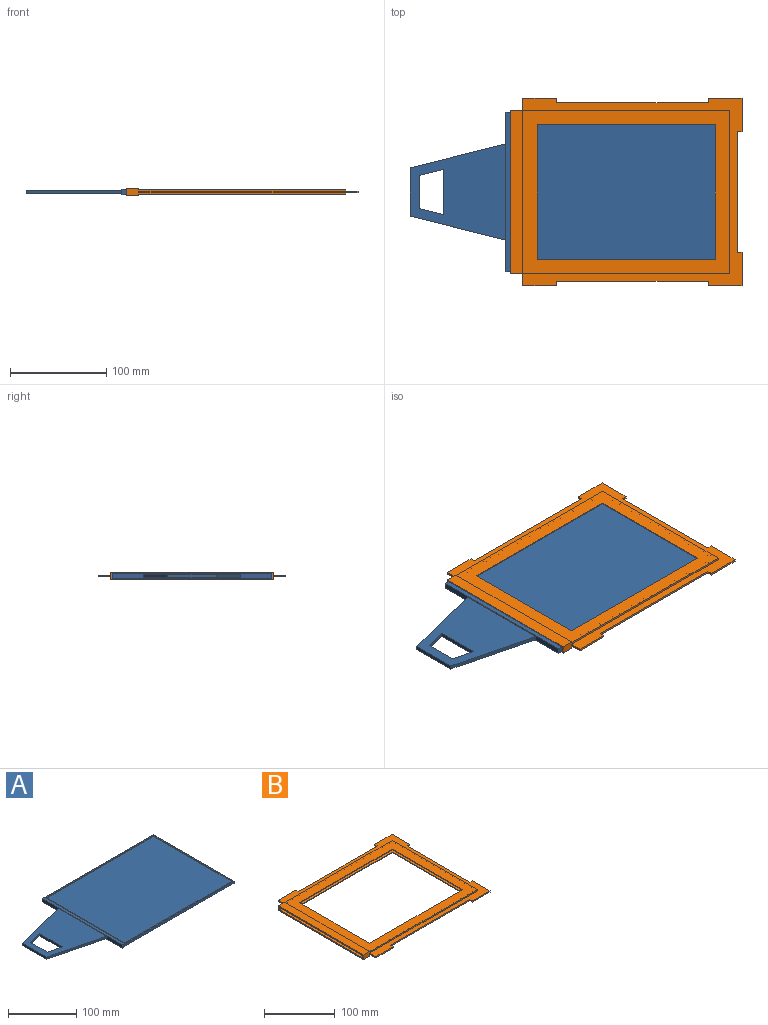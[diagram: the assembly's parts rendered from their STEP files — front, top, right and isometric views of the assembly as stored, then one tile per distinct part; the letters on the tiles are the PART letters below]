
ASSEMBLY  parts=2 mates=1
PART A: 29 faces, bbox 330x166x6 mm
  f0: plane 166x6mm, normal (-1,0,0), area 596mm2, adj f8,f10,f18,f19,f21,f26,f27,f28
  f1: plane 221.5x1mm, normal (0,1,0), area 221.5mm2, adj f2,f4,f12,f14
  f2: plane 162x1mm, normal (-1,0,0), area 162mm2, adj f1,f3,f12,f14
  f3: plane 221.5x1mm, normal (0,-1,0), area 221.5mm2, adj f2,f4,f12,f14
  f4: plane 162x1mm, normal (1,0,0), area 162mm2, adj f1,f3,f12,f14
  f5: plane 162x1mm, normal (-1,0,0), area 162mm2, adj f6,f11,f13,f15
  f6: plane 221.5x1mm, normal (0,1,0), area 221.5mm2, adj f5,f7,f13,f15
  f7: plane 162x1mm, normal (1,0,0), area 162mm2, adj f6,f11,f13,f15
  f8: plane 230.5x6mm, normal (0,-1,0), area 932mm2, adj f0,f9,f12,f13,f16,f17,f18,f19
  f9: plane 166x4mm, normal (1,0,0), area 664mm2, adj f8,f10,f12,f13
  f10: plane 230.5x6mm, normal (0,1,0), area 932mm2, adj f0,f9,f12,f13,f16,f17,f18,f19
  f11: plane 221.5x1mm, normal (0,-1,0), area 221.5mm2, adj f5,f7,f13,f15
  f12: plane 225.5x166mm, normal (0,0,1), area 1550mm2, adj f1,f2,f3,f4,f8,f9,f10,f16
  f13: plane 225.5x166mm, normal (0,0,-1), area 1550mm2, adj f5,f6,f7,f8,f9,f10,f11,f17
  f14: plane 221.5x162mm, normal (0,0,1), area 35883mm2, adj f1,f2,f3,f4
  f15: plane 221.5x162mm, normal (0,0,-1), area 35883mm2, adj f5,f6,f7,f11
  f16: plane 166x1mm, normal (1,0,0), area 166mm2, adj f8,f10,f12,f18
  f17: plane 166x1mm, normal (1,0,0), area 166mm2, adj f8,f10,f13,f19
  f18: plane 166x5mm, normal (0,0,1), area 830mm2, adj f0,f8,f10,f16
  f19: plane 166x5mm, normal (0,0,-1), area 830mm2, adj f0,f8,f10,f17
  f20: plane 50x4mm, normal (-1,0,0), area 200mm2, adj f21,f26,f27,f28
  f21: plane 99.5x25mm, normal (-0.24,-0.97,0), area 410.4mm2, adj f0,f20,f27,f28
  f22: plane 25x6.28mm, normal (0.24,-0.97,0), area 103.1mm2, adj f23,f25,f27,f28
  f23: plane 46.97x4mm, normal (-1,0,0), area 187.9mm2, adj f22,f24,f27,f28
  f24: plane 25x6.28mm, normal (0.24,0.97,0), area 103.1mm2, adj f23,f25,f27,f28
  f25: plane 34.4x4mm, normal (1,0,0), area 137.6mm2, adj f22,f24,f27,f28
  f26: plane 99.5x25mm, normal (-0.24,0.97,0), area 410.4mm2, adj f0,f20,f27,f28
  f27: plane 100x99.5mm, normal (0,0,1), area 6445.4mm2, adj f0,f20,f21,f22,f23,f24,f25,f26
  f28: plane 100x99.5mm, normal (0,0,-1), area 6445.4mm2, adj f0,f20,f21,f22,f23,f24,f25,f26
PART B: 43 faces, bbox 240x195x8 mm
  f0: plane 140x1mm, normal (-1,0,0), area 140mm2, adj f1,f3,f12,f39
  f1: plane 185x1mm, normal (0,1,0), area 185mm2, adj f0,f2,f12,f39
  f2: plane 140x1mm, normal (1,0,0), area 140mm2, adj f1,f3,f12,f39
  f3: plane 185x1mm, normal (0,-1,0), area 185mm2, adj f0,f2,f12,f39
  f4: plane 170x2mm, normal (1,0,0), area 340mm2, adj f5,f6,f13,f37
  f5: plane 227.5x8mm, normal (0,-1,0), area 960mm2, adj f4,f10,f12,f13,f14,f15,f16,f17
  f6: plane 227.5x8mm, normal (0,1,0), area 960mm2, adj f4,f10,f12,f13,f14,f15,f16,f17
  f7: plane 140x1mm, normal (-1,0,0), area 140mm2, adj f8,f11,f13,f38
  f8: plane 185x1mm, normal (0,1,0), area 185mm2, adj f7,f9,f13,f38
  f9: plane 140x1mm, normal (1,0,0), area 140mm2, adj f8,f11,f13,f38
  f10: plane 170x2mm, normal (1,0,0), area 340mm2, adj f5,f6,f12,f36
  f11: plane 185x1mm, normal (0,-1,0), area 185mm2, adj f7,f9,f13,f38
  f12: plane 215x170mm, normal (0,0,1), area 10650mm2, adj f0,f1,f2,f3,f5,f6,f10,f14
  f13: plane 215x170mm, normal (0,0,-1), area 10650mm2, adj f4,f5,f6,f7,f8,f9,f11,f15
  f14: plane 170x1mm, normal (1,0,0), area 170mm2, adj f5,f6,f12,f17
  f15: plane 170x1mm, normal (1,0,0), area 170mm2, adj f5,f6,f13,f18
  f16: plane 170x8mm, normal (-1,0,0), area 696mm2, adj f5,f6,f17,f18,f38,f39,f40,f41
  f17: plane 170x12.5mm, normal (0,0,1), area 2125mm2, adj f5,f6,f14,f16
  f18: plane 170x12.5mm, normal (0,0,-1), area 2125mm2, adj f5,f6,f15,f16
  f19: plane 12.5x2mm, normal (-1,0,0), area 25mm2, adj f5,f20,f36,f37
  f20: plane 35x2mm, normal (0,-1,0), area 70mm2, adj f19,f21,f36,f37
  f21: plane 5x2mm, normal (1,0,0), area 10mm2, adj f20,f22,f36,f37
  f22: plane 157.5x2mm, normal (0,-1,0), area 315mm2, adj f21,f23,f36,f37
  f23: plane 5x2mm, normal (-1,0,0), area 10mm2, adj f22,f24,f36,f37
  f24: plane 35x2mm, normal (0,-1,0), area 70mm2, adj f23,f25,f36,f37
  f25: plane 35x2mm, normal (1,0,0), area 70mm2, adj f24,f26,f36,f37
  f26: plane 5x2mm, normal (0,1,0), area 10mm2, adj f25,f27,f36,f37
  f27: plane 125x2mm, normal (1,0,0), area 250mm2, adj f26,f28,f36,f37
  f28: plane 5x2mm, normal (0,-1,0), area 10mm2, adj f27,f29,f36,f37
  f29: plane 35x2mm, normal (1,0,0), area 70mm2, adj f28,f30,f36,f37
  f30: plane 35x2mm, normal (0,1,0), area 70mm2, adj f29,f31,f36,f37
  f31: plane 5x2mm, normal (-1,0,0), area 10mm2, adj f30,f32,f36,f37
  f32: plane 157.5x2mm, normal (0,1,0), area 315mm2, adj f31,f33,f36,f37
  f33: plane 5x2mm, normal (1,0,0), area 10mm2, adj f32,f34,f36,f37
  f34: plane 35x2mm, normal (0,1,0), area 70mm2, adj f33,f35,f36,f37
  f35: plane 12.5x2mm, normal (-1,0,0), area 25mm2, adj f6,f34,f36,f37
  f36: plane 227.5x195mm, normal (0,0,1), area 5612.5mm2, adj f5,f6,f10,f19,f20,f21,f22,f23
  f37: plane 227.5x195mm, normal (0,0,-1), area 5612.5mm2, adj f4,f5,f6,f19,f20,f21,f22,f23
  f38: plane 225.5x166mm, normal (0,0,1), area 11533mm2, adj f7,f8,f9,f11,f16,f40,f41,f42
  f39: plane 225.5x166mm, normal (0,0,-1), area 11533mm2, adj f0,f1,f2,f3,f16,f40,f41,f42
  f40: plane 225.5x4mm, normal (0,-1,0), area 902mm2, adj f16,f38,f39,f42
  f41: plane 225.5x4mm, normal (0,1,0), area 902mm2, adj f16,f38,f39,f42
  f42: plane 166x4mm, normal (-1,0,0), area 664mm2, adj f38,f39,f40,f41
PLACE A t=(-7.25,0,0)mm
PLACE B at identity fixed
MATE slider A.f17 <-> B.f16  axis (-1,0,0) through (-120,-83,-2)mm
